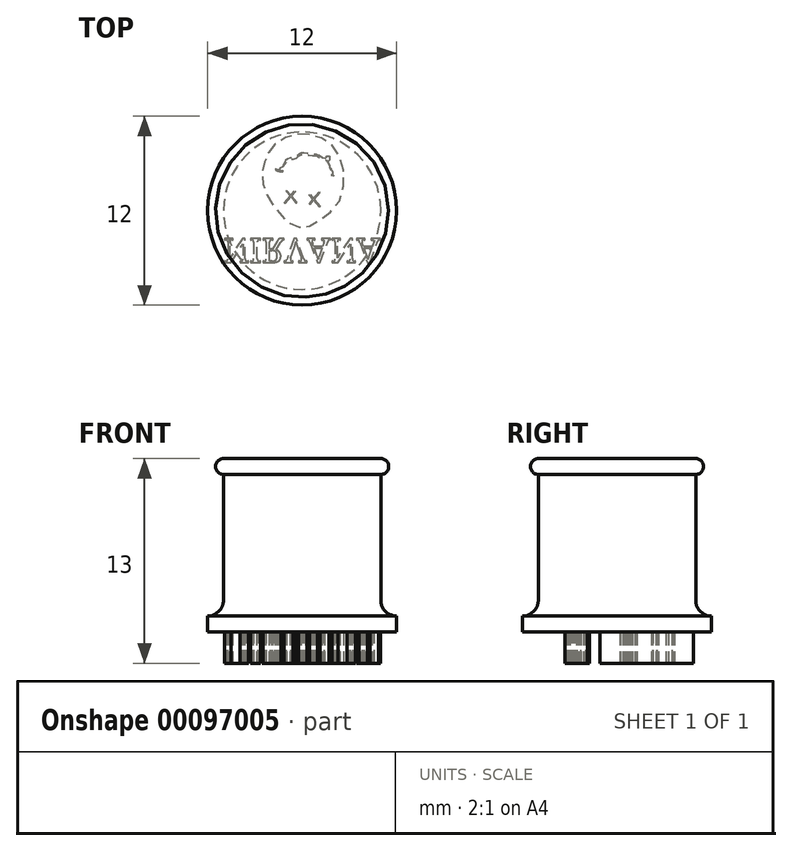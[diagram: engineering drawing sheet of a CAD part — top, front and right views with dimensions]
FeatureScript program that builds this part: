
annotation { "Feature Type Name" : "Feature", "Feature Type Description" : "" }
export const myFeature = defineFeature(function(context is Context, id is Id, definition is map)
    precondition{}
    {
        {
            var Q0;
            Q0=qCreatedBy(makeId("Top.planeOp"),FACE);
            var sketch = newSketch(context, id + "F0", { "sketchPlane" : qUnion([Q0])});
            skCircle(sketch, "E0", {"center": v(0, 0) * mm, "radius": 5 * mm});
            skSolve(sketch);
        }
        {
            var Q0;
            Q0 = qSketchRegion(id + "F0", true);
            extrude(context, id + "F1", {"entities" : qUnion([Q0]), "depth" : 11 * mm});
        }
        {
            var Q0;
            Q0=qCreatedBy(makeId("Top.planeOp"),FACE);
            var sketch = newSketch(context, id + "F2", { "sketchPlane" : qUnion([Q0])});
            skCircle(sketch, "E1", {"center": v(0, 0) * mm, "radius": 6 * mm});
            skSolve(sketch);
        }
        {
            var Q0;
            Q0 = qSketchRegion(id + "F2", true);
            extrude(context, id + "F3", {"entities" : qUnion([Q0]), "operationType" : NewBodyOperationType.ADD, "depth" : 1 * mm});
        }
        {
            var Q0;
            Q0=makeQuery(id+"F3.boolean.opBoolean","INTERSECT",EDGE,{"derivedFrom":[makeQuery(id+"F1.opExtrude","SWEPT_FACE",FACE,{"disambiguationData":[OSD([sQuery(id+"F0.wireOp",EDGE,"E0")])]}),makeQuery(id+"F3.opExtrude","CAP_FACE",FACE,{"disambiguationData":[OSD([sQuery(id+"F2.wireOp",EDGE,"E1")])],"isStart":false})]});
            fillet(context, id + "F4", {"entities" : qUnion([Q0]), "radius" : 1 * mm, "tangentPropagation" : true, "allowEdgeOverflow" : false});
        }
        {
            var Q0;
            Q0=qCreatedBy(makeId("Right.planeOp"),FACE);
            var sketch = newSketch(context, id + "F5", { "sketchPlane" : qUnion([Q0])});
            skArc(sketch, "E2", {"start": v(-5, 11) * mm, "mid": v(-5.5, 10.5) * mm, "end": v(-5, 10) * mm});
            skLineSegment(sketch, "E3", {"start": v(-5, 11) * mm, "end": v(-5, 10) * mm});
            skLineSegment(sketch, "E4", {"start": v(0, 13.6) * mm, "end": v(0, 5.95) * mm, "construction": true});
            skSolve(sketch);
        }
        {
            var Q0;
            Q0 = qSketchRegion(id + "F5", true);
            var Q1;
            Q1=sQuery(id+"F5.wireOp",EDGE,"E4");
            revolve(context, id + "F6", {"operationType" : NewBodyOperationType.ADD, "entities" : qUnion([Q0]), "axis" : qUnion([Q1]), "revolveType" : RevolveType.FULL});
        }
        {
            var Q0;
            Q0=makeQuery(id+"F3.boolean.opBoolean","MERGE",FACE,{"derivedFrom":[makeQuery(id+"F1.opExtrude","CAP_FACE",FACE,{"disambiguationData":[OSD([sQuery(id+"F0.wireOp",EDGE,"E0")])],"isStart":true}),makeQuery(id+"F3.opExtrude","CAP_FACE",FACE,{"disambiguationData":[OSD([sQuery(id+"F2.wireOp",EDGE,"E1")])],"isStart":true})]});
            var sketch = newSketch(context, id + "F7", { "sketchPlane" : qUnion([Q0])});
            skText(sketch, "E5", { "text": "NIRVANA", "fontName": "NotoSerif-Regular.ttf"});
            skFitSpline(sketch, "E6", {"points": [v(-1.7, -3.88) * mm, v(-0.7, -4.55) * mm, v(0.54, -4.58) * mm, v(1.71, -4.05) * mm, v(2.42, -2.6) * mm, v(2.12, -0.6) * mm, v(0, 0.81) * mm, v(-1, 0.38) * mm, v(-1.64, -0.4) * mm, v(-2.1, -1.06) * mm, v(-2.38, -2.27) * mm, v(-2.14, -3.14) * mm, v(-1.7, -3.88) * mm]});
            skFitSpline(sketch, "E7", {"points": [v(-1.44, -2.54) * mm, v(-1.21, -2.78) * mm, v(-0.93, -3.2) * mm, v(-0.44, -3.3) * mm, v(-0.1, -3.56) * mm, v(0.47, -3.51) * mm, v(0.9, -3.48) * mm, v(1.26, -3.3) * mm, v(1.55, -3.2) * mm, v(1.71, -2.87) * mm, v(1.8, -2.63) * mm, v(1.93, -2.27) * mm], "startDerivative": vector(-1.01, -10) * mm, "endDerivative": vector(-3.03, 6.06) * mm});
            skFitSpline(sketch, "E8", {"points": [v(-1.65, -2.67) * mm, v(-1.6, -2.6) * mm, v(-1.44, -2.54) * mm, v(-1.35, -2.54) * mm, v(-1.21, -2.54) * mm], "startDerivative": vector(0.15, 0.38) * mm, "endDerivative": vector(0.56, 0) * mm});
            skFitSpline(sketch, "E9", {"points": [v(1.93, -2.27) * mm, v(1.95, -2.26) * mm, v(1.97, -2.24) * mm, v(2, -2.21) * mm], "startDerivative": vector(0.08, 0.05) * mm, "endDerivative": vector(0.06, 0.07) * mm});
            skFitSpline(sketch, "E10", {"points": [v(1.93, -2.27) * mm, v(1.9, -2.27) * mm, v(1.89, -2.27) * mm, v(1.88, -2.27) * mm, v(1.88, -2.27) * mm, v(1.87, -2.27) * mm, v(1.86, -2.27) * mm, v(1.85, -2.26) * mm, v(1.85, -2.26) * mm], "startDerivative": vector(-0.14, -0.04) * mm, "endDerivative": vector(-0.05, -0.02) * mm});
            skLineSegment(sketch, "E11", {"start": v(-1.65, -2.67) * mm, "end": v(-1.7, -2.64) * mm});
            skFitSpline(sketch, "E12", {"points": [v(-1.7, -2.64) * mm, v(-1.69, -2.6) * mm, v(-1.67, -2.58) * mm, v(-1.64, -2.56) * mm, v(-1.61, -2.54) * mm, v(-1.59, -2.53) * mm, v(-1.56, -2.52) * mm, v(-1.54, -2.52) * mm, v(-1.51, -2.5) * mm, v(-1.49, -2.5) * mm, v(-1.44, -2.5) * mm, v(-1.42, -2.5) * mm, v(-1.39, -2.5) * mm, v(-1.35, -2.5) * mm, v(-1.32, -2.49) * mm, v(-1.3, -2.49) * mm, v(-1.26, -2.49) * mm, v(-1.23, -2.49) * mm, v(-1.22, -2.5) * mm, v(-1.21, -2.54) * mm], "startDerivative": vector(0.34, 0.6) * mm, "endDerivative": vector(0.04, -0.96) * mm});
            skFitSpline(sketch, "E13", {"points": [v(-2.24, -0.99) * mm, v(-1.8, -0.31) * mm, v(-1.44, 0.16) * mm, v(-1, 0.64) * mm, v(0, 1.07) * mm, v(1.06, 0.64) * mm, v(2.3, -0.52) * mm, v(2.6, -2.66) * mm, v(1.88, -4.19) * mm, v(0.58, -4.8) * mm, v(-0.72, -4.77) * mm, v(-1.88, -4.05) * mm, v(-2.33, -3.23) * mm, v(-2.55, -2.24) * mm, v(-2.24, -0.99) * mm]});
            skFitSpline(sketch, "E14", {"points": [v(1.85, -2.26) * mm, v(1.85, -2.25) * mm, v(1.86, -2.26) * mm, v(1.86, -2.26) * mm, v(1.86, -2.26) * mm, v(1.86, -2.26) * mm, v(1.87, -2.26) * mm, v(1.87, -2.26) * mm, v(1.88, -2.26) * mm, v(1.88, -2.26) * mm, v(1.89, -2.26) * mm, v(1.9, -2.26) * mm, v(1.9, -2.26) * mm, v(1.9, -2.26) * mm, v(1.9, -2.26) * mm, v(1.9, -2.26) * mm, v(1.92, -2.26) * mm, v(1.93, -2.26) * mm, v(1.93, -2.26) * mm, v(1.93, -2.26) * mm, v(1.94, -2.26) * mm, v(1.95, -2.25) * mm, v(1.95, -2.25) * mm, v(1.96, -2.25) * mm, v(1.96, -2.24) * mm, v(1.96, -2.24) * mm, v(1.97, -2.23) * mm, v(1.97, -2.23) * mm, v(1.98, -2.22) * mm, v(1.98, -2.22) * mm, v(1.98, -2.21) * mm, v(1.99, -2.21) * mm, v(2, -2.21) * mm], "startDerivative": vector(0.04, 0.2) * mm, "endDerivative": vector(0.18, -0.14) * mm});
            skFitSpline(sketch, "E15", {"points": [v(1.94, -2.26) * mm, v(1.95, -2.28) * mm, v(1.95, -2.3) * mm, v(1.95, -2.3) * mm, v(1.96, -2.31) * mm, v(1.96, -2.33) * mm, v(1.96, -2.34) * mm, v(1.97, -2.35) * mm, v(1.97, -2.37) * mm, v(1.97, -2.38) * mm, v(1.97, -2.4) * mm, v(1.97, -2.4) * mm, v(1.97, -2.42) * mm, v(1.97, -2.43) * mm, v(1.96, -2.44) * mm, v(1.94, -2.5) * mm, v(1.94, -2.53) * mm, v(1.9, -2.54) * mm, v(1.9, -2.57) * mm, v(1.88, -2.59) * mm, v(1.86, -2.63) * mm, v(1.82, -2.67) * mm, v(1.8, -2.7) * mm, v(1.78, -2.76) * mm, v(1.77, -2.79) * mm, v(1.76, -2.83) * mm, v(1.75, -2.9) * mm, v(1.73, -2.93) * mm, v(1.73, -2.96) * mm, v(1.72, -3) * mm, v(1.7, -3.03) * mm, v(1.7, -3.06) * mm, v(1.67, -3.14) * mm, v(1.46, -3.3) * mm, v(1.4, -3.31) * mm, v(1.34, -3.33) * mm, v(1.3, -3.35) * mm, v(1.23, -3.38) * mm, v(1.2, -3.4) * mm, v(1.16, -3.44) * mm, v(1.12, -3.46) * mm, v(1.07, -3.48) * mm, v(1.07, -3.5) * mm, v(1, -3.53) * mm, v(0.9, -3.55) * mm, v(0.87, -3.57) * mm, v(0.77, -3.57) * mm, v(0.68, -3.6) * mm, v(0.64, -3.6) * mm, v(0.5, -3.6) * mm, v(0.43, -3.61) * mm, v(0.31, -3.63) * mm, v(0.21, -3.65) * mm, v(0.15, -3.67) * mm, v(0.08, -3.67) * mm, v(0, -3.67) * mm, v(-0.13, -3.63) * mm, v(-0.16, -3.61) * mm, v(-0.2, -3.6) * mm, v(-0.23, -3.57) * mm, v(-0.25, -3.55) * mm, v(-0.29, -3.51) * mm, v(-0.32, -3.49) * mm, v(-0.35, -3.45) * mm, v(-0.42, -3.42) * mm, v(-0.45, -3.4) * mm, v(-0.52, -3.38) * mm, v(-0.6, -3.36) * mm, v(-0.66, -3.34) * mm, v(-0.74, -3.33) * mm, v(-0.8, -3.32) * mm, v(-0.85, -3.31) * mm, v(-0.96, -3.27) * mm, v(-0.99, -3.24) * mm, v(-1.04, -3.2) * mm, v(-1.05, -3.2) * mm, v(-1.07, -3.13) * mm, v(-1.1, -3.06) * mm, v(-1.12, -3.02) * mm, v(-1.13, -3) * mm, v(-1.14, -2.98) * mm, v(-1.16, -2.96) * mm, v(-1.17, -2.93) * mm, v(-1.19, -2.9) * mm, v(-1.21, -2.87) * mm, v(-1.23, -2.86) * mm, v(-1.25, -2.85) * mm, v(-1.28, -2.85) * mm, v(-1.3, -2.84) * mm, v(-1.34, -2.81) * mm, v(-1.42, -2.79) * mm, v(-1.45, -2.77) * mm, v(-1.47, -2.74) * mm, v(-1.49, -2.69) * mm, v(-1.49, -2.67) * mm, v(-1.49, -2.64) * mm, v(-1.5, -2.63) * mm, v(-1.5, -2.6) * mm, v(-1.5, -2.6) * mm, v(-1.5, -2.57) * mm, v(-1.5, -2.55) * mm, v(-1.5, -2.55) * mm], "startDerivative": vector(1.46, -3.01) * mm, "endDerivative": vector(0.55, -0.12) * mm});
            skLineSegment(sketch, "E16", {"start": v(-1.02, -1.26) * mm, "end": v(-0.75, -0.93) * mm});
            skLineSegment(sketch, "E17", {"start": v(-0.37, -0.49) * mm, "end": v(-0.33, -0.52) * mm});
            skLineSegment(sketch, "E18", {"start": v(-0.33, -0.52) * mm, "end": v(-0.68, -0.93) * mm});
            skLineSegment(sketch, "E19", {"start": v(-0.98, -1.29) * mm, "end": v(-1.02, -1.26) * mm});
            skLineSegment(sketch, "E20.bottom", {"start": v(-1.12, -0.5) * mm, "end": v(-1.08, -0.46) * mm});
            skLineSegment(sketch, "E20.top", {"start": v(-0.47, -1.26) * mm, "end": v(-0.44, -1.23) * mm});
            skLineSegment(sketch, "E20.left", {"start": v(-1.12, -0.5) * mm, "end": v(-0.75, -0.93) * mm});
            skLineSegment(sketch, "E20.right", {"start": v(-1.08, -0.46) * mm, "end": v(-0.71, -0.9) * mm});
            skLineSegment(sketch, "E21.bottom", {"start": v(0.45, -0.43) * mm, "end": v(0.5, -0.4) * mm});
            skLineSegment(sketch, "E21.top", {"start": v(1.1, -1.2) * mm, "end": v(1.14, -1.16) * mm});
            skLineSegment(sketch, "E21.left", {"start": v(0.45, -0.43) * mm, "end": v(0.69, -0.7) * mm});
            skLineSegment(sketch, "E21.right", {"start": v(0.5, -0.4) * mm, "end": v(0.72, -0.67) * mm});
            skLineSegment(sketch, "E22.bottom", {"start": v(0.45, -1) * mm, "end": v(0.69, -0.7) * mm});
            skLineSegment(sketch, "E22.top", {"start": v(0.49, -1.02) * mm, "end": v(0.72, -0.75) * mm});
            skLineSegment(sketch, "E22.left", {"start": v(0.45, -1) * mm, "end": v(0.49, -1.02) * mm});
            skLineSegment(sketch, "E22.right", {"start": v(1.1, -0.22) * mm, "end": v(1.13, -0.26) * mm});
            skFitSpline(sketch, "E23", {"points": [v(1.46, -3.3) * mm, v(1.49, -3.36) * mm, v(1.52, -3.4) * mm, v(1.55, -3.43) * mm, v(1.57, -3.48) * mm, v(1.62, -3.48) * mm, v(1.67, -3.48) * mm, v(1.72, -3.48) * mm, v(1.74, -3.44) * mm, v(1.74, -3.42) * mm, v(1.74, -3.4) * mm, v(1.75, -3.35) * mm, v(1.75, -3.3) * mm, v(1.74, -3.25) * mm, v(1.73, -3.2) * mm, v(1.67, -3.14) * mm], "startDerivative": vector(0.37, -0.8) * mm, "endDerivative": vector(-0.78, 0.76) * mm});
            skLineSegment(sketch, "E24.trimOffspring", {"start": v(0.72, -0.75) * mm, "end": v(1.1, -1.2) * mm});
            skLineSegment(sketch, "E25.trimOffspring", {"start": v(0.75, -0.7) * mm, "end": v(1.14, -1.16) * mm});
            skLineSegment(sketch, "E26.trimOffspring", {"start": v(0.72, -0.67) * mm, "end": v(1.1, -0.22) * mm});
            skLineSegment(sketch, "E27.trimOffspring", {"start": v(0.75, -0.7) * mm, "end": v(1.13, -0.26) * mm});
            skLineSegment(sketch, "E28.trimOffspring", {"start": v(-0.71, -0.97) * mm, "end": v(-0.47, -1.26) * mm});
            skLineSegment(sketch, "E29.trimOffspring", {"start": v(-0.71, -0.97) * mm, "end": v(-0.98, -1.29) * mm});
            skLineSegment(sketch, "E30.trimOffspring", {"start": v(-0.68, -0.93) * mm, "end": v(-0.44, -1.23) * mm});
            skLineSegment(sketch, "E31.trimOffspring", {"start": v(-0.71, -0.9) * mm, "end": v(-0.37, -0.49) * mm});
            skFitSpline(sketch, "E32", {"points": [v(1.57, -3.24) * mm, v(1.58, -3.26) * mm, v(1.58, -3.28) * mm, v(1.59, -3.3) * mm, v(1.59, -3.3) * mm, v(1.6, -3.32) * mm, v(1.6, -3.33) * mm, v(1.6, -3.35) * mm, v(1.61, -3.37) * mm, v(1.62, -3.37) * mm, v(1.62, -3.37) * mm], "startDerivative": vector(0.07, -0.16) * mm, "endDerivative": vector(0.03, 0) * mm});
            skFitSpline(sketch, "E33", {"points": [v(1.62, -3.37) * mm, v(1.63, -3.37) * mm, v(1.63, -3.37) * mm, v(1.63, -3.35) * mm, v(1.63, -3.34) * mm, v(1.63, -3.33) * mm, v(1.62, -3.31) * mm, v(1.62, -3.28) * mm, v(1.6, -3.26) * mm, v(1.6, -3.24) * mm, v(1.59, -3.22) * mm, v(1.59, -3.22) * mm], "startDerivative": vector(0.14, -0.03) * mm, "endDerivative": vector(-0.04, -0.06) * mm});
            const initialGuessF7  = {"E5": [-0.005, 0.00176, 1, 0, 0.00155]};
            skSetInitialGuess(sketch, initialGuessF7);
            skSolve(sketch);
        }
        {
            var Q0;
            Q0 = qSketchRegion(id + "F7", true);
            var Q1;
            Q1=makeQuery(id+"F7.imprint","IMPRINT",FACE,{"disambiguationData":[TD([[makeQuery(id+"F7.imprint","IMPRINT",EDGE,{"derivedFrom":sQuery(id+"F7.wireOp",EDGE,"E6")}),1.0]])]});
            extrude(context, id + "F8", {"entities" : qUnion([Q0, Q1]), "operationType" : NewBodyOperationType.ADD, "depth" : 2 * mm});
        }
    });
